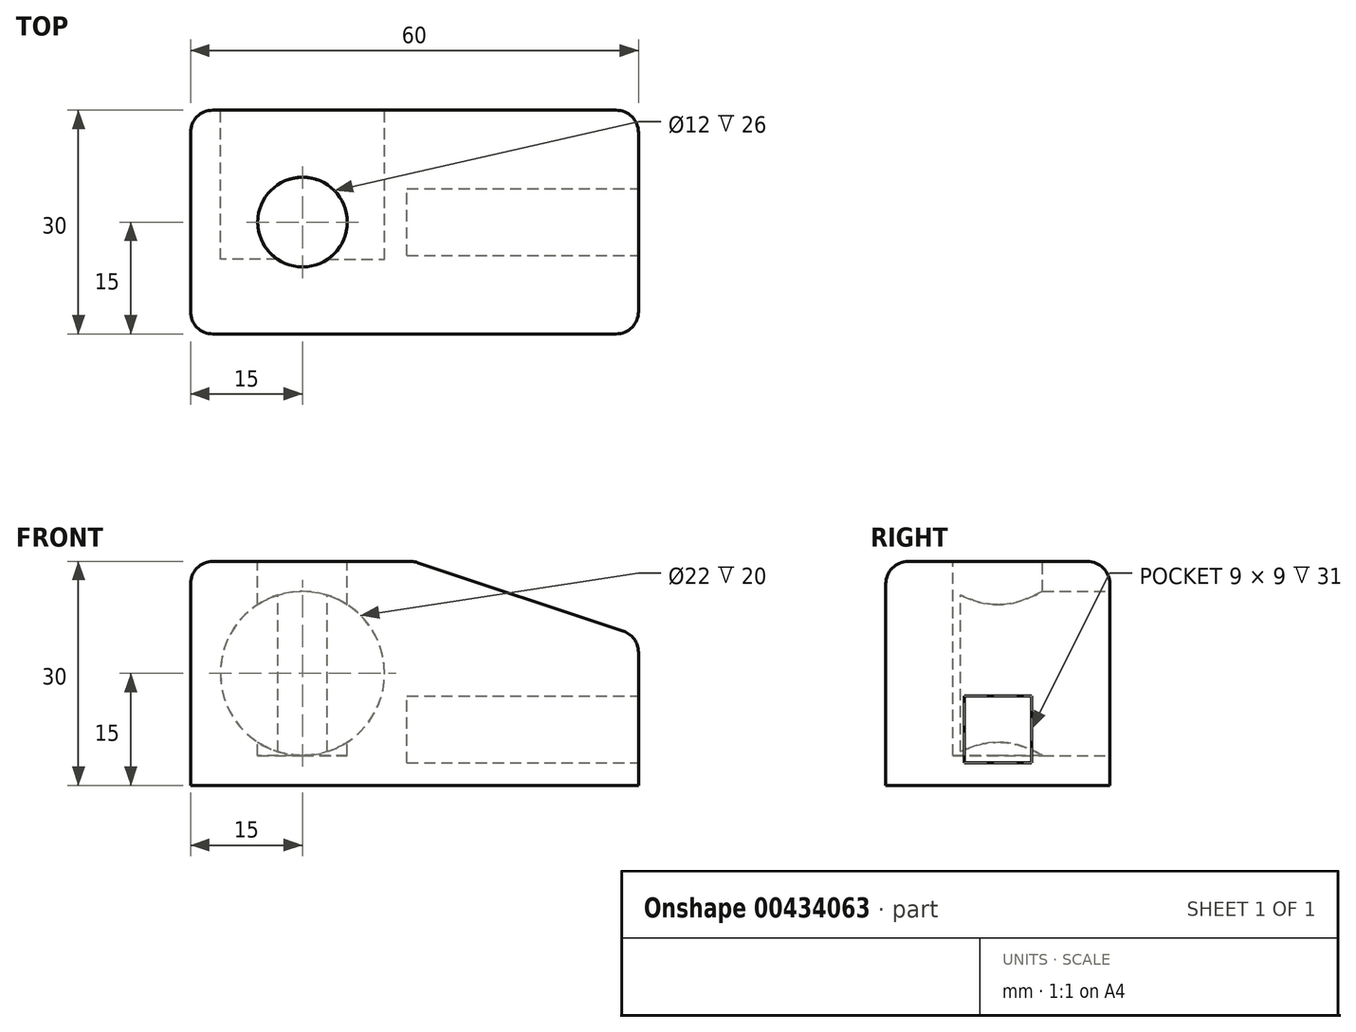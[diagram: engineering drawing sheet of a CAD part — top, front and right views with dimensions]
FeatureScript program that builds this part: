
annotation { "Feature Type Name" : "Feature", "Feature Type Description" : "" }
export const myFeature = defineFeature(function(context is Context, id is Id, definition is map)
    precondition{}
    {
        {
            var Q0;
            Q0=qCreatedBy(makeId("Front.planeOp"),FACE);
            var sketch = newSketch(context, id + "F0", { "sketchPlane" : qUnion([Q0])});
            skLineSegment(sketch, "E0.bottom", {"start": v(30, -15) * mm, "end": v(-30, -15) * mm});
            skLineSegment(sketch, "E0.top", {"start": v(30, 15) * mm, "end": v(-30, 15) * mm});
            skLineSegment(sketch, "E0.left", {"start": v(30, -15) * mm, "end": v(30, 15) * mm});
            skLineSegment(sketch, "E0.right", {"start": v(-30, -15) * mm, "end": v(-30, 15) * mm});
            skPoint(sketch, "E0.middle", {"position": v(0, 0) * mm});
            skSolve(sketch);
        }
        {
            var Q0;
            Q0=makeQuery(id+"F0.imprint","IMPRINT",FACE,{"disambiguationData":[TD([[makeQuery(id+"F0.imprint","IMPRINT",EDGE,{"derivedFrom":sQuery(id+"F0.wireOp",EDGE,"E0.bottom")}),-1.0]])]});
            extrude(context, id + "F1", {"entities" : qUnion([Q0]), "depth" : 30 * mm});
        }
        {
            var Q0;
            Q0=makeQuery(id+"F1.opExtrude","CAP_FACE",FACE,{"disambiguationData":[OSD([sQuery(id+"F0.wireOp",EDGE,"E0.bottom"),sQuery(id+"F0.wireOp",EDGE,"E0.top"),sQuery(id+"F0.wireOp",EDGE,"E0.left"),sQuery(id+"F0.wireOp",EDGE,"E0.right")])],"isStart":false});
            var sketch = newSketch(context, id + "F2", { "sketchPlane" : qUnion([Q0])});
            skLineSegment(sketch, "E1", {"start": v(0, 0) * mm, "end": v(-15, 0) * mm, "construction": true});
            skCircle(sketch, "E2", {"center": v(-15, 0) * mm, "radius": 11 * mm});
            skSolve(sketch);
        }
        {
            var Q0;
            Q0=makeQuery(id+"F2.imprint","IMPRINT",FACE,{"disambiguationData":[TD([[makeQuery(id+"F2.imprint","IMPRINT",EDGE,{"derivedFrom":sQuery(id+"F2.wireOp",EDGE,"E2")}),1.0]])]});
            extrude(context, id + "F3", {"entities" : qUnion([Q0]), "operationType" : NewBodyOperationType.REMOVE, "oppositeDirection" : true, "depth" : 20 * mm});
        }
        {
            var Q0;
            Q0=makeQuery(id+"F1.opExtrude","SWEPT_FACE",FACE,{"disambiguationData":[OSD([sQuery(id+"F0.wireOp",EDGE,"E0.left")])]});
            var sketch = newSketch(context, id + "F4", { "sketchPlane" : qUnion([Q0])});
            skLineSegment(sketch, "E3", {"start": v(-30, -12) * mm, "end": v(0, -12) * mm, "construction": true});
            skLineSegment(sketch, "E4", {"start": v(-15, 15) * mm, "end": v(-15, -15) * mm, "construction": true});
            skLineSegment(sketch, "E5", {"start": v(-19.5, 15) * mm, "end": v(-19.5, -15) * mm, "construction": true});
            skLineSegment(sketch, "E6", {"start": v(-10.5, 15) * mm, "end": v(-10.5, -15) * mm, "construction": true});
            skLineSegment(sketch, "E7", {"start": v(-30, -3) * mm, "end": v(0, -3) * mm, "construction": true});
            skLineSegment(sketch, "E8", {"start": v(-19.5, -12) * mm, "end": v(-19.5, -3) * mm});
            skLineSegment(sketch, "E9", {"start": v(-19.5, -3) * mm, "end": v(-10.5, -3) * mm});
            skLineSegment(sketch, "E10", {"start": v(-10.5, -3) * mm, "end": v(-10.5, -12) * mm});
            skLineSegment(sketch, "E11", {"start": v(-10.5, -12) * mm, "end": v(-19.5, -12) * mm});
            skSolve(sketch);
        }
        {
            var Q0;
            Q0=makeQuery(id+"F4.imprint","IMPRINT",FACE,{"disambiguationData":[TD([[makeQuery(id+"F4.imprint","IMPRINT",EDGE,{"derivedFrom":sQuery(id+"F4.wireOp",EDGE,"E8")}),-1.0]])]});
            extrude(context, id + "F5", {"entities" : qUnion([Q0]), "operationType" : NewBodyOperationType.REMOVE, "oppositeDirection" : true, "depth" : 31 * mm});
        }
        {
            var Q0;
            Q0=makeQuery(id+"F1.opExtrude","SWEPT_FACE",FACE,{"disambiguationData":[OSD([sQuery(id+"F0.wireOp",EDGE,"E0.top")])]});
            var sketch = newSketch(context, id + "F6", { "sketchPlane" : qUnion([Q0])});
            skLineSegment(sketch, "E12", {"start": v(-30, 0) * mm, "end": v(0, -30) * mm, "construction": true});
            skLineSegment(sketch, "E13", {"start": v(0, -30) * mm, "end": v(0, 0) * mm, "construction": true});
            skLineSegment(sketch, "E14", {"start": v(0, 0) * mm, "end": v(-30, -30) * mm, "construction": true});
            skPoint(sketch, "E15", {"position": v(-15, -15) * mm});
            skCircle(sketch, "E16", {"center": v(-15, -15) * mm, "radius": 6 * mm});
            skSolve(sketch);
        }
        {
            var Q0;
            Q0=makeQuery(id+"F6.imprint","IMPRINT",FACE,{"disambiguationData":[TD([[makeQuery(id+"F6.imprint","IMPRINT",EDGE,{"derivedFrom":sQuery(id+"F6.wireOp",EDGE,"E16")}),1.0]])]});
            extrude(context, id + "F7", {"entities" : qUnion([Q0]), "operationType" : NewBodyOperationType.REMOVE, "oppositeDirection" : true, "depth" : 26 * mm});
        }
        {
            var Q0;
            Q0=makeQuery(id+"F1.opExtrude","SWEPT_EDGE",EDGE,{"disambiguationData":[OSD([sQuery(id+"F0.wireOp",EDGE,"E0.top"),sQuery(id+"F0.wireOp",EDGE,"E0.left")])]});
            chamfer(context, id + "F8", {"entities" : qUnion([Q0]), "chamferType" : ChamferType.TWO_OFFSETS, "width1" : 30 * mm, "oppositeDirection" : false, "width2" : 10 * mm, "tangentPropagation" : true});
        }
        {
            var Q0;
            Q0=makeQuery(id+"F1.opExtrude","SWEPT_EDGE",EDGE,{"disambiguationData":[OSD([sQuery(id+"F0.wireOp",EDGE,"E0.top"),sQuery(id+"F0.wireOp",EDGE,"E0.right")])]});
            var Q1;
            Q1=makeQuery(id+"F1.opExtrude","CAP_EDGE",EDGE,{"disambiguationData":[OSD([sQuery(id+"F0.wireOp",EDGE,"E0.top")])],"isStart":true});
            var Q2;
            {var subQ0=sQuery(id+"F0.wireOp",EDGE,"E0.top");Q2=makeQuery(id+"F8.opChamfer","BLEND_EDGE",EDGE,{"blendedFrom":[makeQuery(id+"F1.opExtrude","SWEPT_EDGE",EDGE,{"disambiguationData":[OSD([subQ0,sQuery(id+"F0.wireOp",EDGE,"E0.left")])]}),makeQuery(id+"F1.opExtrude","SWEPT_FACE",FACE,{"disambiguationData":[OSD([subQ0])]})],"blendedInto":[makeQuery(id+"F1.opExtrude","SWEPT_FACE",FACE,{"disambiguationData":[OSD([subQ0])]})]});}
            var Q3;
            {var subQ0=sQuery(id+"F0.wireOp",EDGE,"E0.left");Q3=makeQuery(id+"F8.opChamfer","BLEND_EDGE",EDGE,{"blendedFrom":[makeQuery(id+"F1.opExtrude","SWEPT_EDGE",EDGE,{"disambiguationData":[OSD([sQuery(id+"F0.wireOp",EDGE,"E0.top"),subQ0])]}),makeQuery(id+"F1.opExtrude","SWEPT_FACE",FACE,{"disambiguationData":[OSD([subQ0])]})],"blendedInto":[makeQuery(id+"F1.opExtrude","SWEPT_FACE",FACE,{"disambiguationData":[OSD([subQ0])]})]});}
            var Q4;
            Q4=makeQuery(id+"F1.opExtrude","CAP_EDGE",EDGE,{"disambiguationData":[OSD([sQuery(id+"F0.wireOp",EDGE,"E0.top")])],"isStart":false});
            var Q5;
            {var subQ0=sQuery(id+"F0.wireOp",EDGE,"E0.left");var subQ1=sQuery(id+"F0.wireOp",EDGE,"E0.top");Q5=makeQuery(id+"F8.opChamfer","BLEND_EDGE",EDGE,{"blendedFrom":[makeQuery(id+"F1.opExtrude","SWEPT_EDGE",EDGE,{"disambiguationData":[OSD([subQ1,subQ0])]}),makeQuery(id+"F1.opExtrude","CAP_FACE",FACE,{"disambiguationData":[OSD([sQuery(id+"F0.wireOp",EDGE,"E0.bottom"),subQ1,subQ0,sQuery(id+"F0.wireOp",EDGE,"E0.right")])],"isStart":false})],"blendedInto":[makeQuery(id+"F1.opExtrude","CAP_FACE",FACE,{"disambiguationData":[OSD([sQuery(id+"F0.wireOp",EDGE,"E0.bottom"),subQ1,subQ0,sQuery(id+"F0.wireOp",EDGE,"E0.right")])],"isStart":false})]});}
            var Q6;
            {var subQ0=sQuery(id+"F0.wireOp",EDGE,"E0.left");var subQ1=sQuery(id+"F0.wireOp",EDGE,"E0.top");Q6=makeQuery(id+"F8.opChamfer","BLEND_EDGE",EDGE,{"blendedFrom":[makeQuery(id+"F1.opExtrude","SWEPT_EDGE",EDGE,{"disambiguationData":[OSD([subQ1,subQ0])]}),makeQuery(id+"F1.opExtrude","CAP_FACE",FACE,{"disambiguationData":[OSD([sQuery(id+"F0.wireOp",EDGE,"E0.bottom"),subQ1,subQ0,sQuery(id+"F0.wireOp",EDGE,"E0.right")])],"isStart":true})],"blendedInto":[makeQuery(id+"F1.opExtrude","CAP_FACE",FACE,{"disambiguationData":[OSD([sQuery(id+"F0.wireOp",EDGE,"E0.bottom"),subQ1,subQ0,sQuery(id+"F0.wireOp",EDGE,"E0.right")])],"isStart":true})]});}
            var Q7;
            Q7=makeQuery(id+"F1.opExtrude","CAP_EDGE",EDGE,{"disambiguationData":[OSD([sQuery(id+"F0.wireOp",EDGE,"E0.left")])],"isStart":false});
            var Q8;
            Q8=makeQuery(id+"F1.opExtrude","CAP_EDGE",EDGE,{"disambiguationData":[OSD([sQuery(id+"F0.wireOp",EDGE,"E0.left")])],"isStart":true});
            var Q9;
            Q9=makeQuery(id+"F1.opExtrude","CAP_EDGE",EDGE,{"disambiguationData":[OSD([sQuery(id+"F0.wireOp",EDGE,"E0.right")])],"isStart":true});
            var Q10;
            Q10=makeQuery(id+"F1.opExtrude","CAP_EDGE",EDGE,{"disambiguationData":[OSD([sQuery(id+"F0.wireOp",EDGE,"E0.right")])],"isStart":false});
            fillet(context, id + "F9", {"entities" : qUnion([Q0, Q1, Q2, Q3, Q4, Q5, Q6, Q7, Q8, Q9, Q10]), "radius" : 3 * mm, "tangentPropagation" : true, "allowEdgeOverflow" : false});
        }
        {
            var Q0;
            Q0=makeQuery(id+"F1.opExtrude","SWEPT_BODY",BODY,{"disambiguationData":[OSD([sQuery(id+"F0.wireOp",EDGE,"E0.bottom"),sQuery(id+"F0.wireOp",EDGE,"E0.top"),sQuery(id+"F0.wireOp",EDGE,"E0.left"),sQuery(id+"F0.wireOp",EDGE,"E0.right")])]});
            var Q1;
            Q1=makeQuery(id+"F2.imprint","IMPRINT",FACE,{"disambiguationData":[TD([[makeQuery(id+"F2.imprint","IMPRINT",EDGE,{"derivedFrom":sQuery(id+"F2.wireOp",EDGE,"E2")}),-1.0]])]});
            mirror(context, id + "F10", {"entities" : qUnion([Q0]), "mirrorPlane" : qUnion([Q1])});
        }
        {
            var Q0;
            Q0=makeQuery(id+"F1.opExtrude","SWEPT_BODY",BODY,{"disambiguationData":[OSD([sQuery(id+"F0.wireOp",EDGE,"E0.bottom"),sQuery(id+"F0.wireOp",EDGE,"E0.top"),sQuery(id+"F0.wireOp",EDGE,"E0.left"),sQuery(id+"F0.wireOp",EDGE,"E0.right")])]});
            deleteBodies(context, id + "F11", {"entities" : qUnion([Q0])});
        }
    });
